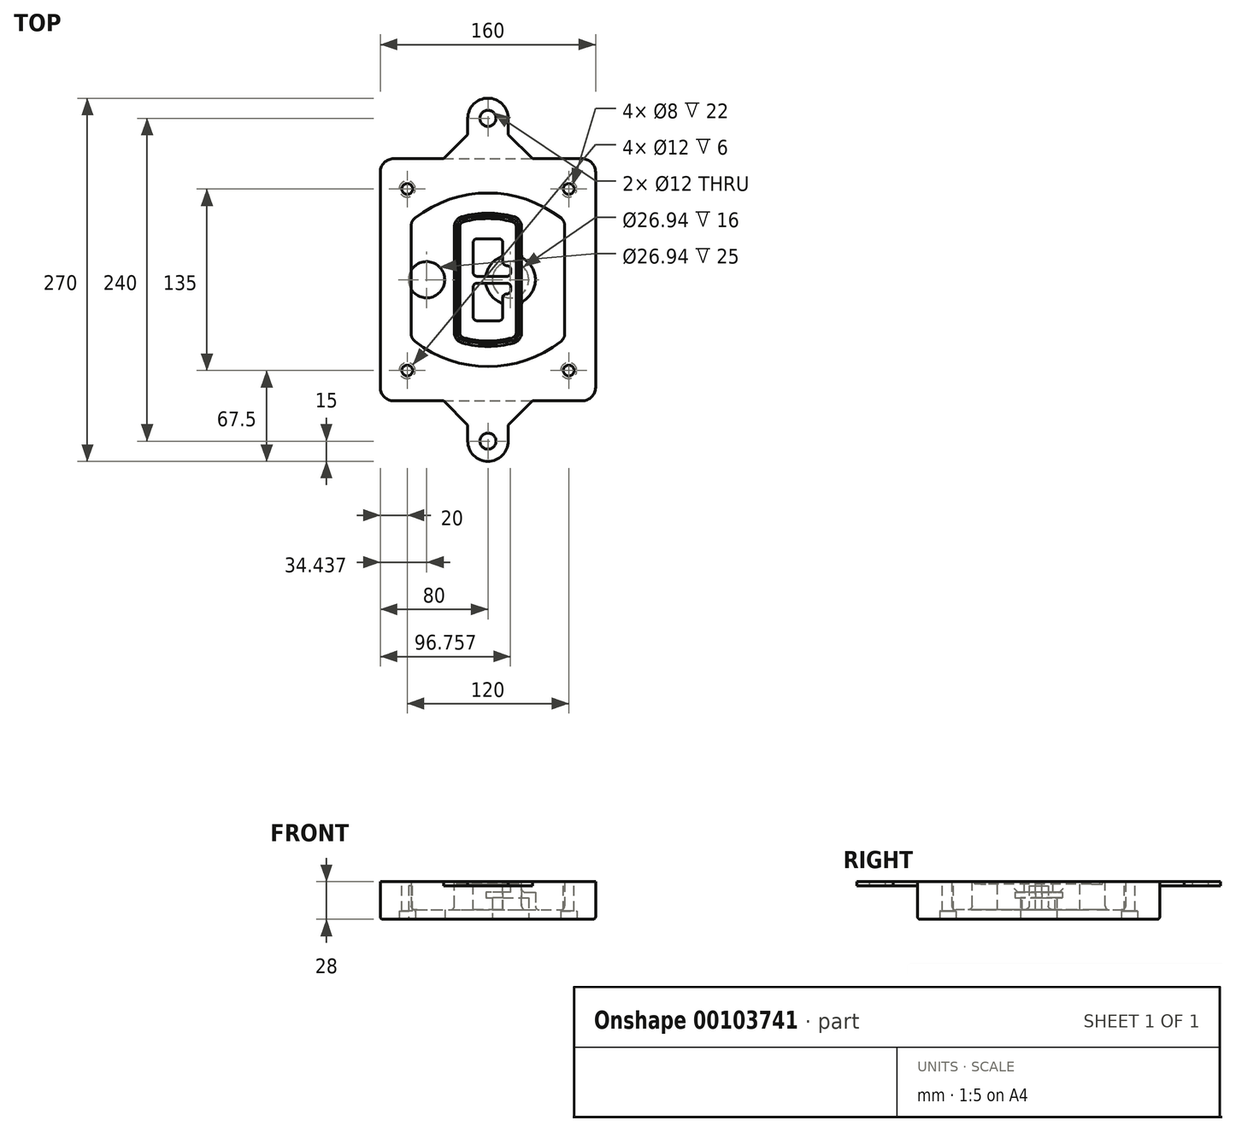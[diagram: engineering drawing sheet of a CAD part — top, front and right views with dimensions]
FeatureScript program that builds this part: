
annotation { "Feature Type Name" : "Feature", "Feature Type Description" : "" }
export const myFeature = defineFeature(function(context is Context, id is Id, definition is map)
    precondition{}
    {
        {
            var Q0;
            Q0=qCreatedBy(makeId("Top.planeOp"),FACE);
            var sketch = newSketch(context, id + "F0", { "sketchPlane" : qUnion([Q0])});
            skPoint(sketch, "E0.rect.middle", {"position": v(0, 0) * mm});
            skLineSegment(sketch, "E1.bottom", {"start": v(-70, -90) * mm, "end": v(70, -90) * mm});
            skLineSegment(sketch, "E1.top", {"start": v(-70, 90) * mm, "end": v(70, 90) * mm});
            skLineSegment(sketch, "E1.left", {"start": v(-80, -80) * mm, "end": v(-80, 80) * mm});
            skLineSegment(sketch, "E1.right", {"start": v(80, -80) * mm, "end": v(80, 80) * mm});
            skLineSegment(sketch, "E2", {"start": v(-80, 90) * mm, "end": v(80, -90) * mm, "construction": true});
            skLineSegment(sketch, "E3", {"start": v(80, 90) * mm, "end": v(-80, -90) * mm, "construction": true});
            skCircle(sketch, "E4", {"center": v(-60, 67.5) * mm, "radius": 4 * mm});
            skCircle(sketch, "E5", {"center": v(60, 67.5) * mm, "radius": 4 * mm});
            skCircle(sketch, "E6", {"center": v(60, -67.5) * mm, "radius": 4 * mm});
            skCircle(sketch, "E7", {"center": v(-60, -67.5) * mm, "radius": 4 * mm});
            skLineSegment(sketch, "E8", {"start": v(-60, 67.5) * mm, "end": v(60, 67.5) * mm, "construction": true});
            skLineSegment(sketch, "E9", {"start": v(60, 67.5) * mm, "end": v(60, -67.5) * mm, "construction": true});
            skLineSegment(sketch, "E10", {"start": v(60, -67.5) * mm, "end": v(-60, -67.5) * mm, "construction": true});
            skLineSegment(sketch, "E11", {"start": v(-60, -67.5) * mm, "end": v(-60, 67.5) * mm, "construction": true});
            skLineSegment(sketch, "E12", {"start": v(-60, 40.3) * mm, "end": v(-60, -40.3) * mm});
            skLineSegment(sketch, "E13", {"start": v(60, 40.3) * mm, "end": v(60, -40.3) * mm});
            skArc(sketch, "E14", {"start": v(56.15, 48.18) * mm, "mid": v(0, 67.5) * mm, "end": v(-56.15, 48.18) * mm});
            skArc(sketch, "E15", {"start": v(-56.15, -48.18) * mm, "mid": v(0, -67.5) * mm, "end": v(56.15, -48.18) * mm});
            skLineSegment(sketch, "E16", {"start": v(-60, 0) * mm, "end": v(60, 0) * mm, "construction": true});
            skPoint(sketch, "E17.visualSharp", {"position": v(-60, -45) * mm});
            skArc(sketch, "E17.filletArc", {"start": v(-60, -40.3) * mm, "mid": v(-58.99, -44.68) * mm, "end": v(-56.15, -48.18) * mm});
            skPoint(sketch, "E18.visualSharp", {"position": v(-60, 45) * mm});
            skArc(sketch, "E18.filletArc", {"start": v(-56.15, 48.18) * mm, "mid": v(-58.99, 44.68) * mm, "end": v(-60, 40.3) * mm});
            skPoint(sketch, "E19.visualSharp", {"position": v(60, 45) * mm});
            skArc(sketch, "E19.filletArc", {"start": v(60, 40.3) * mm, "mid": v(58.99, 44.68) * mm, "end": v(56.15, 48.18) * mm});
            skPoint(sketch, "E20.visualSharp", {"position": v(60, -45) * mm});
            skArc(sketch, "E20.filletArc", {"start": v(56.15, -48.18) * mm, "mid": v(58.99, -44.68) * mm, "end": v(60, -40.3) * mm});
            skPoint(sketch, "E21.visualSharp", {"position": v(-80, 90) * mm});
            skArc(sketch, "E21.filletArc", {"start": v(-70, 90) * mm, "mid": v(-77.07, 87.07) * mm, "end": v(-80, 80) * mm});
            skPoint(sketch, "E22.visualSharp", {"position": v(80, 90) * mm});
            skArc(sketch, "E22.filletArc", {"start": v(80, 80) * mm, "mid": v(77.07, 87.07) * mm, "end": v(70, 90) * mm});
            skPoint(sketch, "E23.visualSharp", {"position": v(80, -90) * mm});
            skArc(sketch, "E23.filletArc", {"start": v(70, -90) * mm, "mid": v(77.07, -87.07) * mm, "end": v(80, -80) * mm});
            skPoint(sketch, "E24.visualSharp", {"position": v(-80, -90) * mm});
            skArc(sketch, "E24.filletArc", {"start": v(-80, -80) * mm, "mid": v(-77.07, -87.07) * mm, "end": v(-70, -90) * mm});
            skArc(sketch, "E25.0", {"start": v(57, 40.3) * mm, "mid": v(56.3, 43.36) * mm, "end": v(54.3, 45.81) * mm});
            skLineSegment(sketch, "E25.1", {"start": v(57, 40.3) * mm, "end": v(57, -40.3) * mm});
            skArc(sketch, "E25.2", {"start": v(54.3, -45.81) * mm, "mid": v(56.3, -43.36) * mm, "end": v(57, -40.3) * mm});
            skArc(sketch, "E25.3", {"start": v(-54.3, -45.81) * mm, "mid": v(0, -64.5) * mm, "end": v(54.3, -45.81) * mm});
            skArc(sketch, "E25.4", {"start": v(-57, -40.3) * mm, "mid": v(-56.3, -43.36) * mm, "end": v(-54.3, -45.81) * mm});
            skArc(sketch, "E25.5", {"start": v(54.3, 45.81) * mm, "mid": v(0, 64.5) * mm, "end": v(-54.3, 45.81) * mm});
            skLineSegment(sketch, "E25.6", {"start": v(-57, 40.3) * mm, "end": v(-57, -40.3) * mm});
            skArc(sketch, "E25.7", {"start": v(-54.3, 45.81) * mm, "mid": v(-56.3, 43.36) * mm, "end": v(-57, 40.3) * mm});
            skArc(sketch, "E26.0", {"start": v(-58.62, 51.33) * mm, "mid": v(-62.58, 46.43) * mm, "end": v(-64, 40.3) * mm});
            skArc(sketch, "E26.1", {"start": v(58.62, 51.33) * mm, "mid": v(0, 71.5) * mm, "end": v(-58.62, 51.33) * mm});
            skArc(sketch, "E26.2", {"start": v(64, 40.3) * mm, "mid": v(62.58, 46.43) * mm, "end": v(58.62, 51.33) * mm});
            skLineSegment(sketch, "E26.3", {"start": v(64, 40.3) * mm, "end": v(64, -40.3) * mm});
            skArc(sketch, "E26.4", {"start": v(58.62, -51.33) * mm, "mid": v(62.58, -46.43) * mm, "end": v(64, -40.3) * mm});
            skLineSegment(sketch, "E26.5", {"start": v(-64, 40.3) * mm, "end": v(-64, -40.3) * mm});
            skArc(sketch, "E26.6", {"start": v(-58.62, -51.33) * mm, "mid": v(0, -71.5) * mm, "end": v(58.62, -51.33) * mm});
            skArc(sketch, "E26.7", {"start": v(-64, -40.3) * mm, "mid": v(-62.58, -46.43) * mm, "end": v(-58.62, -51.33) * mm});
            skSolve(sketch);
        }
        {
            var Q0;
            Q0=makeQuery(id+"F0.imprint","IMPRINT",FACE,{"disambiguationData":[TD([[makeQuery(id+"F0.imprint","IMPRINT",EDGE,{"derivedFrom":sQuery(id+"F0.wireOp",EDGE,"E1.bottom")}),1.0]])]});
            var Q1;
            Q1=makeQuery(id+"F0.imprint","IMPRINT",FACE,{"disambiguationData":[TD([[makeQuery(id+"F0.imprint","IMPRINT",EDGE,{"derivedFrom":sQuery(id+"F0.wireOp",EDGE,"E12")}),1.0]])]});
            var Q2;
            Q2=makeQuery(id+"F0.imprint","IMPRINT",FACE,{"disambiguationData":[TD([[makeQuery(id+"F0.imprint","IMPRINT",EDGE,{"derivedFrom":sQuery(id+"F0.wireOp",EDGE,"E25.0")}),1.0]])]});
            var Q3;
            Q3=makeQuery(id+"F0.imprint","IMPRINT",FACE,{"disambiguationData":[TD([[makeQuery(id+"F0.imprint","IMPRINT",EDGE,{"derivedFrom":sQuery(id+"F0.wireOp",EDGE,"E12")}),-1.0]])]});
            extrude(context, id + "F1", {"entities" : qUnion([Q0, Q1, Q2, Q3]), "oppositeDirection" : true, "depth" : 25 * mm});
        }
        {
            var Q0;
            Q0=makeQuery(id+"F0.imprint","IMPRINT",FACE,{"disambiguationData":[TD([[makeQuery(id+"F0.imprint","IMPRINT",EDGE,{"derivedFrom":sQuery(id+"F0.wireOp",EDGE,"E12")}),1.0]])]});
            extrude(context, id + "F2", {"entities" : qUnion([Q0]), "operationType" : NewBodyOperationType.ADD, "depth" : 3 * mm});
        }
        {
            var Q0;
            Q0=makeQuery(id+"F0.imprint","IMPRINT",FACE,{"disambiguationData":[TD([[makeQuery(id+"F0.imprint","IMPRINT",EDGE,{"derivedFrom":sQuery(id+"F0.wireOp",EDGE,"E25.0")}),1.0]])]});
            extrude(context, id + "F3", {"entities" : qUnion([Q0]), "operationType" : NewBodyOperationType.REMOVE, "oppositeDirection" : true, "depth" : 18 * mm});
        }
        {
            var Q0;
            Q0=makeQuery(id+"F2.opExtrude","CAP_FACE",FACE,{"disambiguationData":[OSD([sQuery(id+"F0.wireOp",EDGE,"E12"),sQuery(id+"F0.wireOp",EDGE,"E13"),sQuery(id+"F0.wireOp",EDGE,"E14"),sQuery(id+"F0.wireOp",EDGE,"E15"),sQuery(id+"F0.wireOp",EDGE,"E17.filletArc"),sQuery(id+"F0.wireOp",EDGE,"E18.filletArc"),sQuery(id+"F0.wireOp",EDGE,"E19.filletArc"),sQuery(id+"F0.wireOp",EDGE,"E20.filletArc"),sQuery(id+"F0.wireOp",EDGE,"E25.0"),sQuery(id+"F0.wireOp",EDGE,"E25.1"),sQuery(id+"F0.wireOp",EDGE,"E25.2"),sQuery(id+"F0.wireOp",EDGE,"E25.3"),sQuery(id+"F0.wireOp",EDGE,"E25.4"),sQuery(id+"F0.wireOp",EDGE,"E25.5"),sQuery(id+"F0.wireOp",EDGE,"E25.6"),sQuery(id+"F0.wireOp",EDGE,"E25.7")])],"isStart":false});
            var sketch = newSketch(context, id + "F4", { "sketchPlane" : qUnion([Q0])});
            skArc(sketch, "E27.0", {"start": v(-19.08, -46.97) * mm, "mid": v(0, -49.5) * mm, "end": v(19.08, -46.97) * mm});
            skArc(sketch, "E28.0", {"start": v(19.08, 46.97) * mm, "mid": v(0, 49.5) * mm, "end": v(-19.08, 46.97) * mm});
            skLineSegment(sketch, "E29", {"start": v(-25, 39.25) * mm, "end": v(-25, -39.25) * mm});
            skLineSegment(sketch, "E30", {"start": v(25, 39.25) * mm, "end": v(25, -39.25) * mm});
            skLineSegment(sketch, "E31", {"start": v(-25, 45.1) * mm, "end": v(25, 45.1) * mm, "construction": true});
            skLineSegment(sketch, "E32", {"start": v(-25, -45.1) * mm, "end": v(25, -45.1) * mm, "construction": true});
            skPoint(sketch, "E33.visualSharp", {"position": v(-25, 45.1) * mm});
            skArc(sketch, "E33.filletArc", {"start": v(-19.08, 46.97) * mm, "mid": v(-23.35, 44.11) * mm, "end": v(-25, 39.25) * mm});
            skPoint(sketch, "E34.visualSharp", {"position": v(25, 45.1) * mm});
            skArc(sketch, "E34.filletArc", {"start": v(25, 39.25) * mm, "mid": v(23.35, 44.11) * mm, "end": v(19.08, 46.97) * mm});
            skPoint(sketch, "E35.visualSharp", {"position": v(25, -45.1) * mm});
            skArc(sketch, "E35.filletArc", {"start": v(19.08, -46.97) * mm, "mid": v(23.35, -44.11) * mm, "end": v(25, -39.25) * mm});
            skPoint(sketch, "E36.visualSharp", {"position": v(-25, -45.1) * mm});
            skArc(sketch, "E36.filletArc", {"start": v(-25, -39.25) * mm, "mid": v(-23.35, -44.11) * mm, "end": v(-19.08, -46.97) * mm});
            skArc(sketch, "E37.0", {"start": v(54.3, 45.81) * mm, "mid": v(0, 64.5) * mm, "end": v(-54.3, 45.81) * mm});
            skArc(sketch, "E37.1", {"start": v(-54.3, 45.81) * mm, "mid": v(-56.3, 43.36) * mm, "end": v(-57, 40.3) * mm});
            skLineSegment(sketch, "E37.2", {"start": v(-57, 40.3) * mm, "end": v(-57, -40.3) * mm});
            skArc(sketch, "E37.3", {"start": v(-57, -40.3) * mm, "mid": v(-56.3, -43.36) * mm, "end": v(-54.3, -45.81) * mm});
            skArc(sketch, "E37.4", {"start": v(-54.3, -45.81) * mm, "mid": v(0, -64.5) * mm, "end": v(54.3, -45.81) * mm});
            skArc(sketch, "E37.5", {"start": v(54.3, -45.81) * mm, "mid": v(56.3, -43.36) * mm, "end": v(57, -40.3) * mm});
            skLineSegment(sketch, "E37.6", {"start": v(57, 40.3) * mm, "end": v(57, -40.3) * mm});
            skArc(sketch, "E37.7", {"start": v(57, 40.3) * mm, "mid": v(56.3, 43.36) * mm, "end": v(54.3, 45.81) * mm});
            skLineSegment(sketch, "E38.0", {"start": v(23, 39.25) * mm, "end": v(23, -39.25) * mm});
            skArc(sketch, "E38.1", {"start": v(18.56, -45.04) * mm, "mid": v(21.76, -42.9) * mm, "end": v(23, -39.25) * mm});
            skArc(sketch, "E38.2", {"start": v(-18.56, -45.04) * mm, "mid": v(0, -47.5) * mm, "end": v(18.56, -45.04) * mm});
            skArc(sketch, "E38.3", {"start": v(-23, -39.25) * mm, "mid": v(-21.76, -42.9) * mm, "end": v(-18.56, -45.04) * mm});
            skLineSegment(sketch, "E38.4", {"start": v(-23, 39.25) * mm, "end": v(-23, -39.25) * mm});
            skArc(sketch, "E38.5", {"start": v(23, 39.25) * mm, "mid": v(21.76, 42.9) * mm, "end": v(18.56, 45.04) * mm});
            skArc(sketch, "E38.6", {"start": v(-18.56, 45.04) * mm, "mid": v(-21.76, 42.9) * mm, "end": v(-23, 39.25) * mm});
            skArc(sketch, "E38.7", {"start": v(18.56, 45.04) * mm, "mid": v(0, 47.5) * mm, "end": v(-18.56, 45.04) * mm});
            skArc(sketch, "E39.0", {"start": v(21, 39.25) * mm, "mid": v(20.18, 41.68) * mm, "end": v(18.04, 43.1) * mm});
            skLineSegment(sketch, "E39.1", {"start": v(21, 39.25) * mm, "end": v(21, -39.25) * mm});
            skArc(sketch, "E39.2", {"start": v(18.04, -43.1) * mm, "mid": v(20.18, -41.68) * mm, "end": v(21, -39.25) * mm});
            skArc(sketch, "E39.3", {"start": v(-18.04, -43.1) * mm, "mid": v(0, -45.5) * mm, "end": v(18.04, -43.1) * mm});
            skArc(sketch, "E39.4", {"start": v(-21, -39.25) * mm, "mid": v(-20.18, -41.68) * mm, "end": v(-18.04, -43.1) * mm});
            skArc(sketch, "E39.5", {"start": v(18.04, 43.1) * mm, "mid": v(0, 45.5) * mm, "end": v(-18.04, 43.1) * mm});
            skLineSegment(sketch, "E39.6", {"start": v(-21, 39.25) * mm, "end": v(-21, -39.25) * mm});
            skArc(sketch, "E39.7", {"start": v(-18.04, 43.1) * mm, "mid": v(-20.18, 41.68) * mm, "end": v(-21, 39.25) * mm});
            skLineSegment(sketch, "E40", {"start": v(-25, 0) * mm, "end": v(25, 0) * mm, "construction": true});
            skLineSegment(sketch, "E41", {"start": v(-11, 5.5) * mm, "end": v(-11, 27.5) * mm});
            skLineSegment(sketch, "E42", {"start": v(-8, 30.5) * mm, "end": v(8, 30.5) * mm});
            skLineSegment(sketch, "E43", {"start": v(11, 27.5) * mm, "end": v(11, 13.5) * mm});
            skLineSegment(sketch, "E44", {"start": v(14, 10.5) * mm, "end": v(14, 10.5) * mm});
            skLineSegment(sketch, "E45", {"start": v(17, 7.5) * mm, "end": v(17, 5.5) * mm});
            skLineSegment(sketch, "E46", {"start": v(14, 2.5) * mm, "end": v(-8, 2.5) * mm});
            skPoint(sketch, "E47.visualSharp", {"position": v(-11, 30.5) * mm});
            skArc(sketch, "E47.filletArc", {"start": v(-8, 30.5) * mm, "mid": v(-10.12, 29.62) * mm, "end": v(-11, 27.5) * mm});
            skPoint(sketch, "E48.visualSharp", {"position": v(11, 30.5) * mm});
            skArc(sketch, "E48.filletArc", {"start": v(11, 27.5) * mm, "mid": v(10.12, 29.62) * mm, "end": v(8, 30.5) * mm});
            skPoint(sketch, "E49.visualSharp", {"position": v(11, 10.5) * mm});
            skArc(sketch, "E49.filletArc", {"start": v(11, 13.5) * mm, "mid": v(11.88, 11.38) * mm, "end": v(14, 10.5) * mm});
            skPoint(sketch, "E50.visualSharp", {"position": v(17, 10.5) * mm});
            skArc(sketch, "E50.filletArc", {"start": v(17, 7.5) * mm, "mid": v(16.12, 9.62) * mm, "end": v(14, 10.5) * mm});
            skPoint(sketch, "E51.visualSharp", {"position": v(17, 2.5) * mm});
            skArc(sketch, "E51.filletArc", {"start": v(14, 2.5) * mm, "mid": v(16.12, 3.38) * mm, "end": v(17, 5.5) * mm});
            skPoint(sketch, "E52.visualSharp", {"position": v(-11, 2.5) * mm});
            skArc(sketch, "E52.filletArc", {"start": v(-11, 5.5) * mm, "mid": v(-10.12, 3.38) * mm, "end": v(-8, 2.5) * mm});
            skLineSegment(sketch, "E53.0.MirrorCS", {"start": v(14, -2.5) * mm, "end": v(-8, -2.5) * mm});
            skArc(sketch, "E54.0.MirrorCS", {"start": v(-11, -5.5) * mm, "mid": v(-10.12, -3.38) * mm, "end": v(-8, -2.5) * mm});
            skLineSegment(sketch, "E55.0.MirrorCS", {"start": v(-11, -5.5) * mm, "end": v(-11, -27.5) * mm});
            skArc(sketch, "E56.0.MirrorCS", {"start": v(-8, -30.5) * mm, "mid": v(-10.12, -29.62) * mm, "end": v(-11, -27.5) * mm});
            skLineSegment(sketch, "E57.0.MirrorCS", {"start": v(-8, -30.5) * mm, "end": v(8, -30.5) * mm});
            skArc(sketch, "E58.0.MirrorCS", {"start": v(11, -27.5) * mm, "mid": v(10.12, -29.62) * mm, "end": v(8, -30.5) * mm});
            skLineSegment(sketch, "E59.0.MirrorCS", {"start": v(11, -27.5) * mm, "end": v(11, -13.5) * mm});
            skArc(sketch, "E60.0.MirrorCS", {"start": v(11, -13.5) * mm, "mid": v(11.88, -11.38) * mm, "end": v(14, -10.5) * mm});
            skArc(sketch, "E61.0.MirrorCS", {"start": v(17, -7.5) * mm, "mid": v(16.12, -9.62) * mm, "end": v(14, -10.5) * mm});
            skLineSegment(sketch, "E62.0.MirrorCS", {"start": v(17, -7.5) * mm, "end": v(17, -5.5) * mm});
            skArc(sketch, "E63.0.MirrorCS", {"start": v(14, -2.5) * mm, "mid": v(16.12, -3.38) * mm, "end": v(17, -5.5) * mm});
            skSolve(sketch);
        }
        {
            var Q0;
            Q0=makeQuery(id+"F4.imprint","IMPRINT",FACE,{"disambiguationData":[TD([[makeQuery(id+"F4.imprint","IMPRINT",EDGE,{"derivedFrom":sQuery(id+"F4.wireOp",EDGE,"E27.0")}),1.0]])]});
            var Q1;
            Q1=makeQuery(id+"F4.imprint","IMPRINT",FACE,{"disambiguationData":[TD([[makeQuery(id+"F4.imprint","IMPRINT",EDGE,{"derivedFrom":sQuery(id+"F4.wireOp",EDGE,"E38.0")}),-1.0]])]});
            var Q2;
            Q2=makeQuery(id+"F4.imprint","IMPRINT",FACE,{"disambiguationData":[TD([[makeQuery(id+"F4.imprint","IMPRINT",EDGE,{"derivedFrom":sQuery(id+"F4.wireOp",EDGE,"E39.0")}),1.0]])]});
            extrude(context, id + "F5", {"entities" : qUnion([Q0, Q1, Q2]), "operationType" : NewBodyOperationType.ADD, "endBound" : BoundingType.UP_TO_NEXT, "oppositeDirection" : true, "depth" : 25 * mm});
        }
        {
            var Q0;
            Q0=makeQuery(id+"F4.imprint","IMPRINT",FACE,{"disambiguationData":[TD([[makeQuery(id+"F4.imprint","IMPRINT",EDGE,{"derivedFrom":sQuery(id+"F4.wireOp",EDGE,"E38.0")}),-1.0]])]});
            extrude(context, id + "F6", {"entities" : qUnion([Q0]), "operationType" : NewBodyOperationType.REMOVE, "oppositeDirection" : true, "depth" : 2 * mm});
        }
        {
            var Q0;
            Q0=makeQuery(id+"F1.opExtrude","CAP_FACE",FACE,{"disambiguationData":[OSD([sQuery(id+"F0.wireOp",EDGE,"E1.bottom"),sQuery(id+"F0.wireOp",EDGE,"E1.top"),sQuery(id+"F0.wireOp",EDGE,"E1.left"),sQuery(id+"F0.wireOp",EDGE,"E1.right"),sQuery(id+"F0.wireOp",EDGE,"E4"),sQuery(id+"F0.wireOp",EDGE,"E5"),sQuery(id+"F0.wireOp",EDGE,"E6"),sQuery(id+"F0.wireOp",EDGE,"E7"),sQuery(id+"F0.wireOp",EDGE,"E21.filletArc"),sQuery(id+"F0.wireOp",EDGE,"E22.filletArc"),sQuery(id+"F0.wireOp",EDGE,"E23.filletArc"),sQuery(id+"F0.wireOp",EDGE,"E24.filletArc")])],"isStart":false});
            var sketch = newSketch(context, id + "F7", { "sketchPlane" : qUnion([Q0])});
            skCircle(sketch, "E64", {"center": v(16.76, 0) * mm, "radius": 13.47 * mm});
            skCircle(sketch, "E65", {"center": v(-45.56, 0) * mm, "radius": 13.47 * mm});
            skLineSegment(sketch, "E66", {"start": v(80, 0) * mm, "end": v(-80, 0) * mm});
            skCircle(sketch, "E67", {"center": v(16.76, 0) * mm, "radius": 18.47 * mm});
            skCircle(sketch, "E68", {"center": v(60, -67.5) * mm, "radius": 6 * mm});
            skCircle(sketch, "E69", {"center": v(-60, -67.5) * mm, "radius": 6 * mm});
            skCircle(sketch, "E70", {"center": v(-60, 67.5) * mm, "radius": 6 * mm});
            skCircle(sketch, "E71", {"center": v(60, 67.5) * mm, "radius": 6 * mm});
            skSolve(sketch);
        }
        {
            var Q0;
            {var subQ1=sQuery(id+"F7.wireOp",EDGE,"E66");var subQ4=sQuery(id+"F7.wireOp",EDGE,"E64");var subQ6=makeQuery(id+"F7.imprint","INTERSECT",VERTEX,{"disambiguationData":[OD(0.0)],"derivedFrom":[subQ4,subQ1]});Q0=makeQuery(id+"F7.imprint","IMPRINT",FACE,{"disambiguationData":[TD([[makeQuery(id+"F7.imprint","IMPRINT",EDGE,{"disambiguationData":[TD([[subQ6,-1.0]])],"derivedFrom":subQ4}),-1.0]])]});}
            var Q1;
            {var subQ0=sQuery(id+"F7.wireOp",EDGE,"E66");var subQ1=sQuery(id+"F7.wireOp",EDGE,"E64");var subQ3=makeQuery(id+"F7.imprint","INTERSECT",VERTEX,{"disambiguationData":[OD(0.0)],"derivedFrom":[subQ1,subQ0]});Q1=makeQuery(id+"F7.imprint","IMPRINT",FACE,{"disambiguationData":[TD([[makeQuery(id+"F7.imprint","IMPRINT",EDGE,{"disambiguationData":[TD([[subQ3,-1.0]])],"derivedFrom":subQ1}),1.0]])]});}
            var Q2;
            {var subQ0=sQuery(id+"F7.wireOp",EDGE,"E66");var subQ1=sQuery(id+"F7.wireOp",EDGE,"E64");var subQ3=makeQuery(id+"F7.imprint","INTERSECT",VERTEX,{"disambiguationData":[OD(0.0)],"derivedFrom":[subQ1,subQ0]});Q2=makeQuery(id+"F7.imprint","IMPRINT",FACE,{"disambiguationData":[TD([[makeQuery(id+"F7.imprint","IMPRINT",EDGE,{"disambiguationData":[TD([[subQ3,1.0]])],"derivedFrom":subQ1}),1.0]])]});}
            var Q3;
            {var subQ1=sQuery(id+"F7.wireOp",EDGE,"E66");var subQ4=sQuery(id+"F7.wireOp",EDGE,"E64");var subQ6=makeQuery(id+"F7.imprint","INTERSECT",VERTEX,{"disambiguationData":[OD(0.0)],"derivedFrom":[subQ4,subQ1]});Q3=makeQuery(id+"F7.imprint","IMPRINT",FACE,{"disambiguationData":[TD([[makeQuery(id+"F7.imprint","IMPRINT",EDGE,{"disambiguationData":[TD([[subQ6,1.0]])],"derivedFrom":subQ4}),-1.0]])]});}
            extrude(context, id + "F8", {"entities" : qUnion([Q0, Q1, Q2, Q3]), "operationType" : NewBodyOperationType.ADD, "oppositeDirection" : true, "depth" : 20 * mm});
        }
        {
            var Q0;
            {var subQ0=sQuery(id+"F7.wireOp",EDGE,"E66");var subQ1=sQuery(id+"F7.wireOp",EDGE,"E64");var subQ3=makeQuery(id+"F7.imprint","INTERSECT",VERTEX,{"disambiguationData":[OD(0.0)],"derivedFrom":[subQ1,subQ0]});Q0=makeQuery(id+"F7.imprint","IMPRINT",FACE,{"disambiguationData":[TD([[makeQuery(id+"F7.imprint","IMPRINT",EDGE,{"disambiguationData":[TD([[subQ3,-1.0]])],"derivedFrom":subQ1}),1.0]])]});}
            var Q1;
            {var subQ0=sQuery(id+"F7.wireOp",EDGE,"E66");var subQ1=sQuery(id+"F7.wireOp",EDGE,"E64");var subQ3=makeQuery(id+"F7.imprint","INTERSECT",VERTEX,{"disambiguationData":[OD(0.0)],"derivedFrom":[subQ1,subQ0]});Q1=makeQuery(id+"F7.imprint","IMPRINT",FACE,{"disambiguationData":[TD([[makeQuery(id+"F7.imprint","IMPRINT",EDGE,{"disambiguationData":[TD([[subQ3,1.0]])],"derivedFrom":subQ1}),1.0]])]});}
            extrude(context, id + "F9", {"entities" : qUnion([Q0, Q1]), "operationType" : NewBodyOperationType.REMOVE, "oppositeDirection" : true, "depth" : 16 * mm});
        }
        {
            var Q0;
            {var subQ0=sQuery(id+"F7.wireOp",EDGE,"E66");var subQ1=sQuery(id+"F7.wireOp",EDGE,"E65");var subQ3=makeQuery(id+"F7.imprint","INTERSECT",VERTEX,{"disambiguationData":[OD(0.0)],"derivedFrom":[subQ1,subQ0]});Q0=makeQuery(id+"F7.imprint","IMPRINT",FACE,{"disambiguationData":[TD([[makeQuery(id+"F7.imprint","IMPRINT",EDGE,{"disambiguationData":[TD([[subQ3,-1.0]])],"derivedFrom":subQ1}),1.0]])]});}
            var Q1;
            {var subQ0=sQuery(id+"F7.wireOp",EDGE,"E66");var subQ1=sQuery(id+"F7.wireOp",EDGE,"E65");var subQ3=makeQuery(id+"F7.imprint","INTERSECT",VERTEX,{"disambiguationData":[OD(0.0)],"derivedFrom":[subQ1,subQ0]});Q1=makeQuery(id+"F7.imprint","IMPRINT",FACE,{"disambiguationData":[TD([[makeQuery(id+"F7.imprint","IMPRINT",EDGE,{"disambiguationData":[TD([[subQ3,1.0]])],"derivedFrom":subQ1}),1.0]])]});}
            extrude(context, id + "F10", {"entities" : qUnion([Q0, Q1]), "operationType" : NewBodyOperationType.REMOVE, "oppositeDirection" : true, "depth" : 25 * mm});
        }
        {
            var Q0;
            Q0=makeQuery(id+"F7.imprint","IMPRINT",FACE,{"disambiguationData":[TD([[makeQuery(id+"F7.imprint","IMPRINT",EDGE,{"derivedFrom":sQuery(id+"F7.wireOp",EDGE,"E68")}),1.0]])]});
            var Q1;
            Q1=makeQuery(id+"F7.imprint","IMPRINT",FACE,{"disambiguationData":[TD([[makeQuery(id+"F7.imprint","IMPRINT",EDGE,{"derivedFrom":makeQuery(id+"F1.opExtrude","CAP_EDGE",EDGE,{"disambiguationData":[OSD([sQuery(id+"F0.wireOp",EDGE,"E5")])],"isStart":false})}),-1.0]])]});
            var Q2;
            Q2=makeQuery(id+"F7.imprint","IMPRINT",FACE,{"disambiguationData":[TD([[makeQuery(id+"F7.imprint","IMPRINT",EDGE,{"derivedFrom":sQuery(id+"F7.wireOp",EDGE,"E69")}),1.0]])]});
            var Q3;
            Q3=makeQuery(id+"F7.imprint","IMPRINT",FACE,{"disambiguationData":[TD([[makeQuery(id+"F7.imprint","IMPRINT",EDGE,{"derivedFrom":makeQuery(id+"F1.opExtrude","CAP_EDGE",EDGE,{"disambiguationData":[OSD([sQuery(id+"F0.wireOp",EDGE,"E4")])],"isStart":false})}),-1.0]])]});
            var Q4;
            Q4=makeQuery(id+"F7.imprint","IMPRINT",FACE,{"disambiguationData":[TD([[makeQuery(id+"F7.imprint","IMPRINT",EDGE,{"derivedFrom":sQuery(id+"F7.wireOp",EDGE,"E70")}),1.0]])]});
            var Q5;
            Q5=makeQuery(id+"F7.imprint","IMPRINT",FACE,{"disambiguationData":[TD([[makeQuery(id+"F7.imprint","IMPRINT",EDGE,{"derivedFrom":makeQuery(id+"F1.opExtrude","CAP_EDGE",EDGE,{"disambiguationData":[OSD([sQuery(id+"F0.wireOp",EDGE,"E7")])],"isStart":false})}),-1.0]])]});
            var Q6;
            Q6=makeQuery(id+"F7.imprint","IMPRINT",FACE,{"disambiguationData":[TD([[makeQuery(id+"F7.imprint","IMPRINT",EDGE,{"derivedFrom":sQuery(id+"F7.wireOp",EDGE,"E71")}),1.0]])]});
            var Q7;
            Q7=makeQuery(id+"F7.imprint","IMPRINT",FACE,{"disambiguationData":[TD([[makeQuery(id+"F7.imprint","IMPRINT",EDGE,{"derivedFrom":makeQuery(id+"F1.opExtrude","CAP_EDGE",EDGE,{"disambiguationData":[OSD([sQuery(id+"F0.wireOp",EDGE,"E6")])],"isStart":false})}),-1.0]])]});
            extrude(context, id + "F11", {"entities" : qUnion([Q0, Q1, Q2, Q3, Q4, Q5, Q6, Q7]), "operationType" : NewBodyOperationType.REMOVE, "oppositeDirection" : true, "depth" : 6 * mm});
        }
        {
            var Q0;
            Q0=makeQuery(id+"F9.boolean.opBoolean","COPY",FACE,{"derivedFrom":makeQuery(id+"F9.opExtrude","CAP_FACE",FACE,{"disambiguationData":[OSD([sQuery(id+"F7.wireOp",EDGE,"E64")])],"isStart":false})});
            var sketch = newSketch(context, id + "F12", { "sketchPlane" : qUnion([Q0])});
            skArc(sketch, "E72.0", {"start": v(11, 17.55) * mm, "mid": v(2.57, 11.82) * mm, "end": v(-1.54, 2.5) * mm});
            skArc(sketch, "E72.1", {"start": v(-1.54, -2.5) * mm, "mid": v(2.57, -11.82) * mm, "end": v(11, -17.55) * mm});
            skLineSegment(sketch, "E73", {"start": v(-1.54, -2.5) * mm, "end": v(14, -2.5) * mm});
            skLineSegment(sketch, "E74.0", {"start": v(14, 2.5) * mm, "end": v(-1.54, 2.5) * mm});
            skArc(sketch, "E74.1", {"start": v(14, 2.5) * mm, "mid": v(16.12, 3.38) * mm, "end": v(17, 5.5) * mm});
            skLineSegment(sketch, "E74.2", {"start": v(17, 7.5) * mm, "end": v(17, 5.5) * mm});
            skArc(sketch, "E74.3", {"start": v(17, 7.5) * mm, "mid": v(16.12, 9.62) * mm, "end": v(14, 10.5) * mm});
            skArc(sketch, "E74.4", {"start": v(11, 13.5) * mm, "mid": v(11.88, 11.38) * mm, "end": v(14, 10.5) * mm});
            skLineSegment(sketch, "E74.5", {"start": v(11, 17.55) * mm, "end": v(11, 13.5) * mm});
            skLineSegment(sketch, "E74.7", {"start": v(14, -2.5) * mm, "end": v(-1.54, -2.5) * mm});
            skArc(sketch, "E74.8", {"start": v(14, -2.5) * mm, "mid": v(16.12, -3.38) * mm, "end": v(17, -5.5) * mm});
            skLineSegment(sketch, "E74.9", {"start": v(17, -7.5) * mm, "end": v(17, -5.5) * mm});
            skArc(sketch, "E74.10", {"start": v(17, -7.5) * mm, "mid": v(16.12, -9.62) * mm, "end": v(14, -10.5) * mm});
            skArc(sketch, "E74.11", {"start": v(11, -13.5) * mm, "mid": v(11.88, -11.38) * mm, "end": v(14, -10.5) * mm});
            skLineSegment(sketch, "E74.12", {"start": v(11, -17.55) * mm, "end": v(11, -13.5) * mm});
            skPoint(sketch, "E75.orphan", {"position": v(11, -27.5) * mm});
            skPoint(sketch, "E76.orphan", {"position": v(-8, -2.5) * mm});
            skPoint(sketch, "E77.orphan", {"position": v(-8, 2.5) * mm});
            skPoint(sketch, "E78.orphan", {"position": v(11, 27.5) * mm});
            skSolve(sketch);
        }
        {
            var Q0;
            {var subQ7=sQuery(id+"F12.wireOp",EDGE,"E72.0");var subQ14=sQuery(id+"F12.wireOp",EDGE,"E72.1");var subQ16=sQuery(id+"F12.wireOp",EDGE,"E74.1");var subQ18=sQuery(id+"F12.wireOp",EDGE,"E74.8");Q0=qUnion([makeQuery(id+"F12.imprint","IMPRINT",FACE,{"disambiguationData":[TD([[makeQuery(id+"F12.imprint","IMPRINT",EDGE,{"derivedFrom":subQ7}),1.0]])]}),makeQuery(id+"F12.imprint","IMPRINT",FACE,{"disambiguationData":[TD([[makeQuery(id+"F12.imprint","IMPRINT",EDGE,{"derivedFrom":subQ14}),1.0]])]}),makeQuery(id+"F12.imprint","IMPRINT",FACE,{"disambiguationData":[TD([[makeQuery(id+"F12.imprint","IMPRINT",EDGE,{"derivedFrom":subQ16}),1.0]])]}),makeQuery(id+"F12.imprint","IMPRINT",FACE,{"disambiguationData":[TD([[makeQuery(id+"F12.imprint","IMPRINT",EDGE,{"derivedFrom":subQ18}),-1.0]])]})]);}
            var Q1;
            Q1=makeQuery(id+"F5.boolean.opBoolean","SPLIT",FACE,{"disambiguationData":[TD([makeQuery(id+"F5.opExtrude","SWEPT_FACE",FACE,{"disambiguationData":[OSD([sQuery(id+"F4.wireOp",EDGE,"E41")])]})])],"derivedFrom":makeQuery(id+"F3.boolean.opBoolean","COPY",FACE,{"derivedFrom":makeQuery(id+"F3.opExtrude","CAP_FACE",FACE,{"disambiguationData":[OSD([sQuery(id+"F0.wireOp",EDGE,"E25.0"),sQuery(id+"F0.wireOp",EDGE,"E25.1"),sQuery(id+"F0.wireOp",EDGE,"E25.2"),sQuery(id+"F0.wireOp",EDGE,"E25.3"),sQuery(id+"F0.wireOp",EDGE,"E25.4"),sQuery(id+"F0.wireOp",EDGE,"E25.5"),sQuery(id+"F0.wireOp",EDGE,"E25.6"),sQuery(id+"F0.wireOp",EDGE,"E25.7")])],"isStart":false})})});
            extrude(context, id + "F13", {"entities" : qUnion([Q0]), "operationType" : NewBodyOperationType.REMOVE, "endBound" : BoundingType.UP_TO_SURFACE, "endBoundEntityFace" : qUnion([Q1]), "depth" : 25 * mm});
        }
        {
            var Q0;
            Q0=makeQuery(id+"F3.boolean.opBoolean","COPY",EDGE,{"derivedFrom":makeQuery(id+"F3.opExtrude","CAP_EDGE",EDGE,{"disambiguationData":[OSD([sQuery(id+"F0.wireOp",EDGE,"E25.6")])],"isStart":false})});
            var Q1;
            Q1=makeQuery(id+"F8.boolean.opBoolean","INTERSECT",EDGE,{"derivedFrom":[makeQuery(id+"F5.opExtrude","SWEPT_FACE",FACE,{"disambiguationData":[OSD([sQuery(id+"F4.wireOp",EDGE,"E30")])]}),makeQuery(id+"F8.opExtrude","CAP_FACE",FACE,{"disambiguationData":[OSD([sQuery(id+"F7.wireOp",EDGE,"E67")])],"isStart":false})]});
            var Q2;
            Q2=makeQuery(id+"F8.boolean.opBoolean","INTERSECT",EDGE,{"disambiguationData":[OD(1.0)],"derivedFrom":[makeQuery(id+"F5.opExtrude","SWEPT_FACE",FACE,{"disambiguationData":[OSD([sQuery(id+"F4.wireOp",EDGE,"E30")])]}),makeQuery(id+"F8.opExtrude","SWEPT_FACE",FACE,{"disambiguationData":[OSD([sQuery(id+"F7.wireOp",EDGE,"E67")])]})]});
            var Q3;
            {var subQ0=sQuery(id+"F4.wireOp",EDGE,"E30");Q3=makeQuery(id+"F8.boolean.opBoolean","SPLIT",EDGE,{"disambiguationData":[TD([makeQuery(id+"F5.opExtrude","SWEPT_FACE",FACE,{"disambiguationData":[OSD([sQuery(id+"F4.wireOp",EDGE,"E35.filletArc")])]})])],"derivedFrom":makeQuery(id+"F5.opExtrude","CAP_EDGE",EDGE,{"disambiguationData":[OSD([subQ0])],"isStart":false})});}
            var Q4;
            {var subQ0=sQuery(id+"F0.wireOp",EDGE,"E25.7");var subQ1=sQuery(id+"F0.wireOp",EDGE,"E25.1");var subQ2=sQuery(id+"F0.wireOp",EDGE,"E25.6");var subQ3=sQuery(id+"F0.wireOp",EDGE,"E25.5");var subQ4=sQuery(id+"F0.wireOp",EDGE,"E25.4");var subQ5=sQuery(id+"F0.wireOp",EDGE,"E25.0");var subQ6=sQuery(id+"F0.wireOp",EDGE,"E25.2");var subQ7=sQuery(id+"F0.wireOp",EDGE,"E25.3");Q4=makeQuery(id+"F8.boolean.opBoolean","INTERSECT",EDGE,{"derivedFrom":[makeQuery(id+"F5.boolean.opBoolean","SPLIT",FACE,{"disambiguationData":[TD([makeQuery(id+"F2.opExtrude","SWEPT_FACE",FACE,{"disambiguationData":[OSD([subQ5])]})])],"derivedFrom":makeQuery(id+"F3.boolean.opBoolean","COPY",FACE,{"derivedFrom":makeQuery(id+"F3.opExtrude","CAP_FACE",FACE,{"disambiguationData":[OSD([subQ5,subQ1,subQ6,subQ7,subQ4,subQ3,subQ2,subQ0])],"isStart":false})})}),makeQuery(id+"F8.opExtrude","SWEPT_FACE",FACE,{"disambiguationData":[OSD([sQuery(id+"F7.wireOp",EDGE,"E67")])]})]});}
            var Q5;
            Q5=makeQuery(id+"F8.boolean.opBoolean","INTERSECT",EDGE,{"disambiguationData":[OD(0.0)],"derivedFrom":[makeQuery(id+"F5.opExtrude","SWEPT_FACE",FACE,{"disambiguationData":[OSD([sQuery(id+"F4.wireOp",EDGE,"E30")])]}),makeQuery(id+"F8.opExtrude","SWEPT_FACE",FACE,{"disambiguationData":[OSD([sQuery(id+"F7.wireOp",EDGE,"E67")])]})]});
            fillet(context, id + "F14", {"entities" : qUnion([Q0, Q1, Q2, Q3, Q4, Q5]), "radius" : 3 * mm, "tangentPropagation" : true, "allowEdgeOverflow" : false});
        }
        {
            var Q0;
            Q0=makeQuery(id+"F1.opExtrude","CAP_EDGE",EDGE,{"disambiguationData":[OSD([sQuery(id+"F0.wireOp",EDGE,"E1.bottom")])],"isStart":false});
            fillet(context, id + "F15", {"entities" : qUnion([Q0]), "radius" : 2 * mm, "tangentPropagation" : true, "allowEdgeOverflow" : false});
        }
        {
            var Q0;
            {var subQ0=sQuery(id+"F0.wireOp",EDGE,"E22.filletArc");var subQ1=sQuery(id+"F0.wireOp",EDGE,"E7");var subQ2=sQuery(id+"F0.wireOp",EDGE,"E6");var subQ3=sQuery(id+"F0.wireOp",EDGE,"E5");var subQ4=sQuery(id+"F0.wireOp",EDGE,"E4");var subQ5=sQuery(id+"F0.wireOp",EDGE,"E1.bottom");var subQ6=sQuery(id+"F0.wireOp",EDGE,"E21.filletArc");var subQ7=sQuery(id+"F0.wireOp",EDGE,"E1.top");var subQ8=sQuery(id+"F0.wireOp",EDGE,"E1.left");var subQ9=sQuery(id+"F0.wireOp",EDGE,"E1.right");var subQ10=sQuery(id+"F0.wireOp",EDGE,"E23.filletArc");var subQ11=sQuery(id+"F0.wireOp",EDGE,"E24.filletArc");Q0=makeQuery(id+"F2.boolean.opBoolean","SPLIT",FACE,{"disambiguationData":[TD([makeQuery(id+"F1.opExtrude","SWEPT_FACE",FACE,{"disambiguationData":[OSD([subQ5])]})])],"derivedFrom":makeQuery(id+"F1.opExtrude","CAP_FACE",FACE,{"disambiguationData":[OSD([subQ5,subQ7,subQ8,subQ9,subQ4,subQ3,subQ2,subQ1,subQ6,subQ0,subQ10,subQ11])],"isStart":true})});}
            var sketch = newSketch(context, id + "F16", { "sketchPlane" : qUnion([Q0])});
            skLineSegment(sketch, "E79", {"start": v(0, 90) * mm, "end": v(0, 120) * mm, "construction": true});
            skLineSegment(sketch, "E80", {"start": v(-33, 90) * mm, "end": v(-15, 108) * mm});
            skLineSegment(sketch, "E81", {"start": v(-15, 108) * mm, "end": v(-15, 120) * mm});
            skArc(sketch, "E82", {"start": v(15, 120) * mm, "mid": v(0, 135) * mm, "end": v(-15, 120) * mm});
            skLineSegment(sketch, "E83", {"start": v(15, 120) * mm, "end": v(15, 108) * mm});
            skLineSegment(sketch, "E84", {"start": v(15, 108) * mm, "end": v(33, 90) * mm});
            skCircle(sketch, "E85", {"center": v(0, 120) * mm, "radius": 6 * mm});
            skLineSegment(sketch, "E86", {"start": v(-80, 0) * mm, "end": v(80, 0) * mm, "construction": true});
            skLineSegment(sketch, "E87.MirrorCS", {"start": v(-33, -90) * mm, "end": v(-15, -108) * mm});
            skLineSegment(sketch, "E88.MirrorCS", {"start": v(-15, -108) * mm, "end": v(-15, -120) * mm});
            skArc(sketch, "E89.MirrorCS", {"start": v(15, -120) * mm, "mid": v(0, -135) * mm, "end": v(-15, -120) * mm});
            skCircle(sketch, "E90.MirrorC", {"center": v(0, -120) * mm, "radius": 6 * mm});
            skLineSegment(sketch, "E91.MirrorCS", {"start": v(15, -120) * mm, "end": v(15, -108) * mm});
            skLineSegment(sketch, "E92.MirrorCS", {"start": v(15, -108) * mm, "end": v(33, -90) * mm});
            skLineSegment(sketch, "E93.MirrorCS", {"start": v(0, -90) * mm, "end": v(0, -120) * mm, "construction": true});
            skSolve(sketch);
        }
        {
            var Q0;
            Q0=makeQuery(id+"F16.imprint","IMPRINT",FACE,{"disambiguationData":[TD([[makeQuery(id+"F16.imprint","IMPRINT",EDGE,{"derivedFrom":makeQuery(id+"F1.opExtrude","CAP_EDGE",EDGE,{"disambiguationData":[OSD([sQuery(id+"F0.wireOp",EDGE,"E1.left")])],"isStart":true})}),-1.0]])]});
            var Q1;
            {var subQ0=sQuery(id+"F16.wireOp",EDGE,"E87.MirrorCS");Q1=makeQuery(id+"F16.imprint","IMPRINT",FACE,{"disambiguationData":[TD([[makeQuery(id+"F16.imprint","IMPRINT",EDGE,{"derivedFrom":subQ0}),1.0]])]});}
            var Q2;
            {var subQ0=sQuery(id+"F16.wireOp",EDGE,"E80");Q2=makeQuery(id+"F16.imprint","IMPRINT",FACE,{"disambiguationData":[TD([[makeQuery(id+"F16.imprint","IMPRINT",EDGE,{"derivedFrom":subQ0}),-1.0]])]});}
            var Q3;
            Q3=makeQuery(id+"F2.opExtrude","CAP_FACE",FACE,{"disambiguationData":[OSD([sQuery(id+"F0.wireOp",EDGE,"E12"),sQuery(id+"F0.wireOp",EDGE,"E13"),sQuery(id+"F0.wireOp",EDGE,"E14"),sQuery(id+"F0.wireOp",EDGE,"E15"),sQuery(id+"F0.wireOp",EDGE,"E17.filletArc"),sQuery(id+"F0.wireOp",EDGE,"E18.filletArc"),sQuery(id+"F0.wireOp",EDGE,"E19.filletArc"),sQuery(id+"F0.wireOp",EDGE,"E20.filletArc"),sQuery(id+"F0.wireOp",EDGE,"E25.0"),sQuery(id+"F0.wireOp",EDGE,"E25.1"),sQuery(id+"F0.wireOp",EDGE,"E25.2"),sQuery(id+"F0.wireOp",EDGE,"E25.3"),sQuery(id+"F0.wireOp",EDGE,"E25.4"),sQuery(id+"F0.wireOp",EDGE,"E25.5"),sQuery(id+"F0.wireOp",EDGE,"E25.6"),sQuery(id+"F0.wireOp",EDGE,"E25.7")])],"isStart":false});
            extrude(context, id + "F17", {"entities" : qUnion([Q0, Q1, Q2]), "operationType" : NewBodyOperationType.ADD, "endBound" : BoundingType.UP_TO_SURFACE, "endBoundEntityFace" : qUnion([Q3]), "depth" : 25 * mm});
        }
    });
